# Revit family: DAS200 1AM DX
name_source: partatom
category: Doors
units: mm (PartAtom-declared; Revit-internal decimal feet)

## family parameters
Always vertical = Yes
Cut with Voids When Loaded = No
Host = Wall
OmniClass Number = 23.30.10.00
OmniClass Title = Doors
Room Calculation Point = No
Shared = No

## types (1)
- DAS200 1AM DX
    Auxiliary power = 0.64 A @ 24 Vdc
    BIMobject Category = Sliding
    Brand = Ditec
    Brand url = http://www.ditecentrematic.com
    Calc Width = 1000 mm  [stored 3.28084 ft]
    Description = automation for sliding doors
    Design country = Italy
    Dimensions = 120x185 mm
    Drive type = electromechanical unit
    Edition number = 1
    Endurance test = 1000000 cyrcle
    Frame = Aluminum + Glass
    Height = 2000 mm  [stored 6.56168 ft]
    IFC Classification = Door
    Manufacturer country = China
    Manufacturer name = Entrematic Italy
    Masterformat 2016 Code = 08 01 32
    Masterformat 2016 Description = Operation and Maintenance of Sliding Glass Doors
    Max Operator Length = 6600 mm  [stored 21.6535 ft]
    Max Width = 3240 mm
    Max nominal power = 75 W
    NBS Reference Code = 25-30-20-77
    NBS Reference Description = Sliding Doorset Systems
    OmniClass Code = 23-17 11 00
    OmniClass Description = Doors
    Operating temperature = -20 ° C / +50 ° C
    Operator = Aluminum
    Operator Length = 2300 mm
    Power supply = 100÷240 Vac @ 50/60 MHz
    Product family = Automatic Doors
    Product group = Sliding Automatic Doors
    Protection rating = IP20
    UNSPSC Code = 301715
    Unicalss 2015 Code = Pr 73_30_23_05
    Uniclass 1.4 Code = JL20
    Uniclass 1.4 Description = Doors
    Uniclass 2.0 Code = SS_25-30-20-77
    Uniclass 2.0 Description = Sliding Doorset Systems
    Uniclass 2015 Name = Automatic sliding door operator
    Velocity = 0.7 m/s
    Wall Closure = By host
    Weight = 120.00 kg
    Width = 1000 mm  [stored 3.28084 ft]

note: [stored X ft] marks values corroborated as IEEE doubles in the binary element streams (Revit-internal decimal feet)

## geometry (parser evidence)
native form markers: Sweep x1
no freeform markers — native parametric forms only
